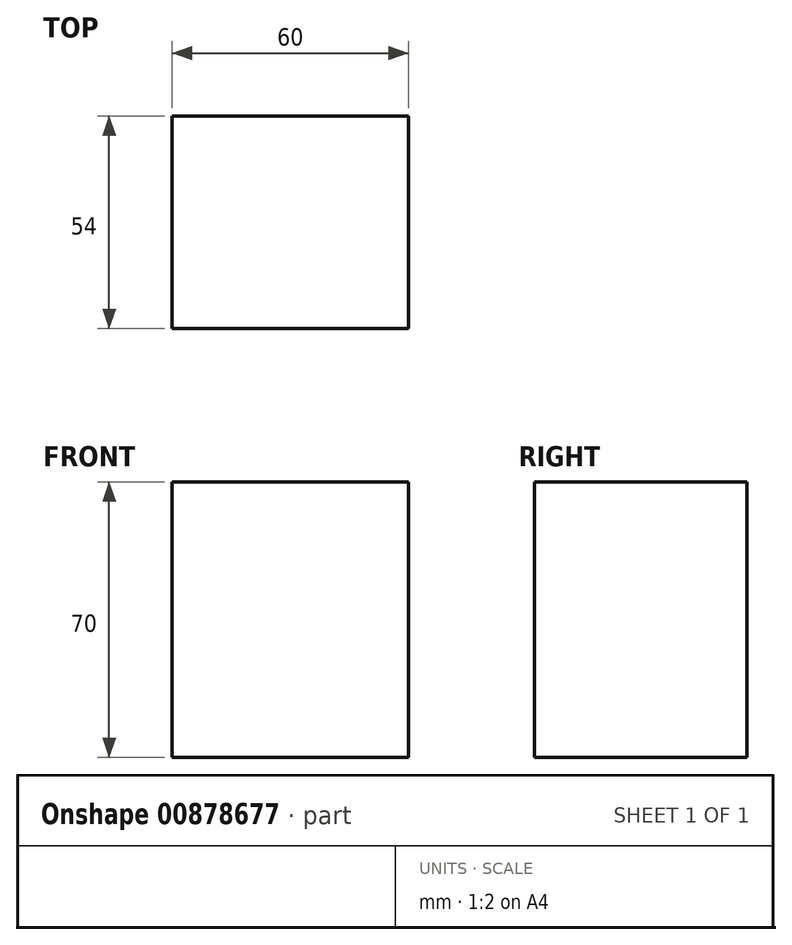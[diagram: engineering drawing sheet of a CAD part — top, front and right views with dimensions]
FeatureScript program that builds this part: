
annotation { "Feature Type Name" : "Feature", "Feature Type Description" : "" }
export const myFeature = defineFeature(function(context is Context, id is Id, definition is map)
    precondition{}
    {
        {
            var Q0;
            Q0=qCreatedBy(makeId("Front.planeOp"),FACE);
            var sketch = newSketch(context, id + "F0", { "sketchPlane" : qUnion([Q0])});
            skLineSegment(sketch, "E0.bottom", {"start": v(-30, 35) * mm, "end": v(30, 35) * mm});
            skLineSegment(sketch, "E0.top", {"start": v(-30, -35) * mm, "end": v(30, -35) * mm});
            skLineSegment(sketch, "E0.left", {"start": v(-30, 35) * mm, "end": v(-30, -35) * mm});
            skLineSegment(sketch, "E0.right", {"start": v(30, 35) * mm, "end": v(30, -35) * mm});
            skPoint(sketch, "E0.middle", {"position": v(0, 0) * mm});
            skSolve(sketch);
        }
        {
            var Q0;
            Q0 = qSketchRegion(id + "F0", true);
            extrude(context, id + "F1", {"entities" : qUnion([Q0]), "depth" : 54 * mm, "offsetDistance" : 25 * mm});
        }
    });
